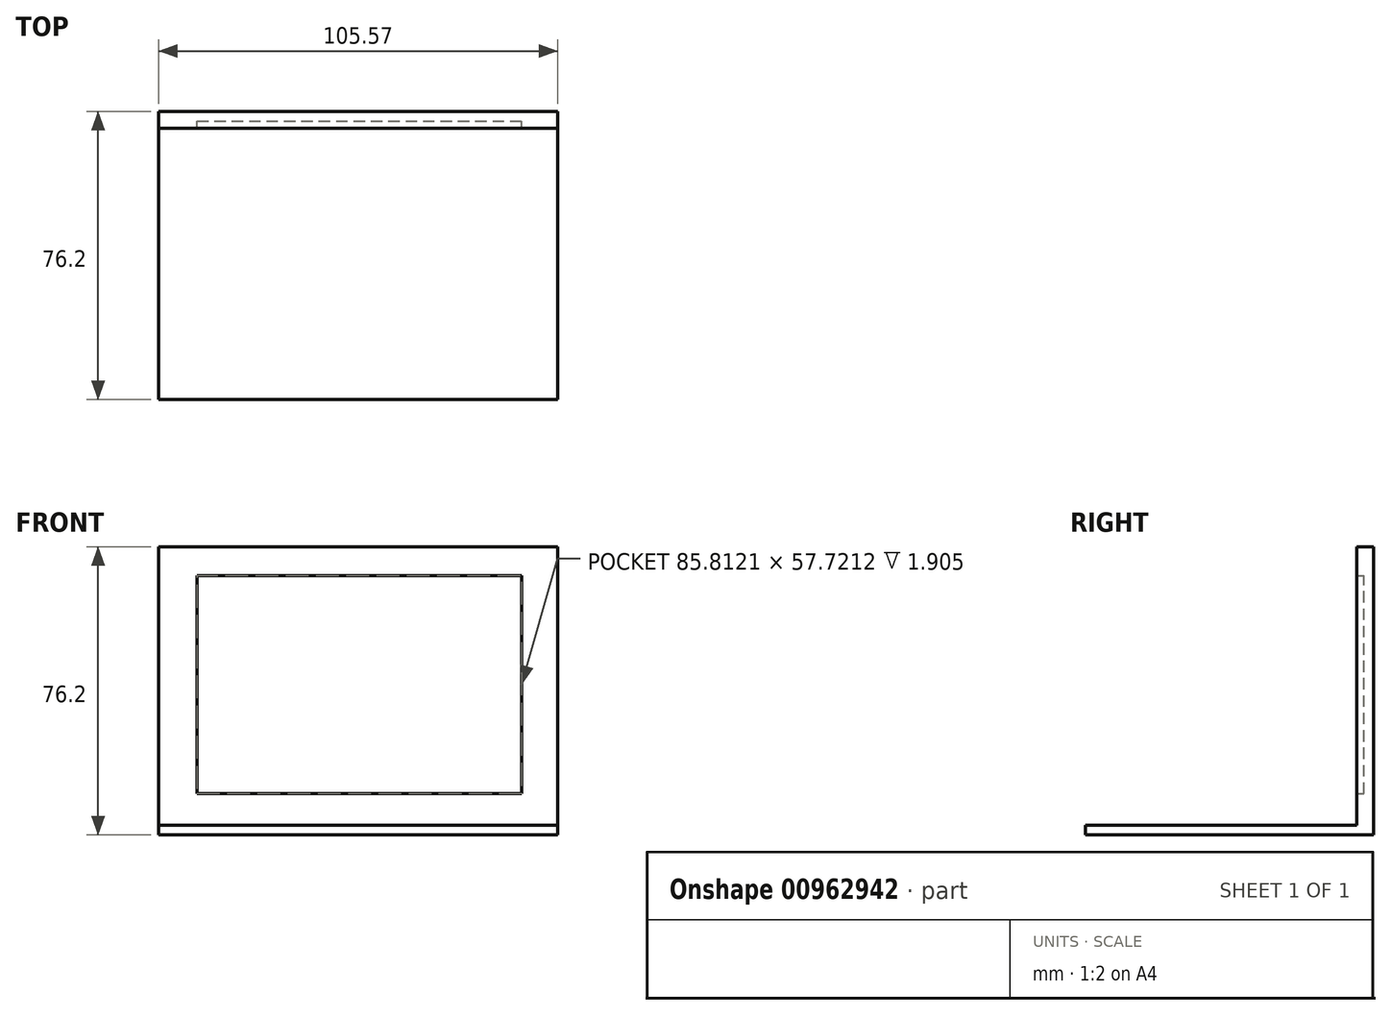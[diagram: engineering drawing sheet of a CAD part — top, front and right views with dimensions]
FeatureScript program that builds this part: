
annotation { "Feature Type Name" : "Feature", "Feature Type Description" : "" }
export const myFeature = defineFeature(function(context is Context, id is Id, definition is map)
    precondition{}
    {
        {
            var Q0;
            Q0=qCreatedBy(makeId("Top.planeOp"),FACE);
            var sketch = newSketch(context, id + "F0", { "sketchPlane" : qUnion([Q0])});
            skLineSegment(sketch, "E0.bottom", {"start": v(-45.25, -76.2) * mm, "end": v(60.32, -76.2) * mm});
            skLineSegment(sketch, "E0.top", {"start": v(-45.25, 0) * mm, "end": v(60.32, 0) * mm});
            skLineSegment(sketch, "E0.left", {"start": v(-45.25, -76.2) * mm, "end": v(-45.25, 0) * mm});
            skLineSegment(sketch, "E0.right", {"start": v(60.32, -76.2) * mm, "end": v(60.32, 0) * mm});
            skSolve(sketch);
        }
        {
            var Q0;
            Q0=makeQuery(id+"F0.imprint","IMPRINT",FACE,{"disambiguationData":[TD([[makeQuery(id+"F0.imprint","IMPRINT",EDGE,{"derivedFrom":sQuery(id+"F0.wireOp",EDGE,"E0.bottom")}),1.0]])]});
            extrude(context, id + "F1", {"entities" : qUnion([Q0]), "depth" : 76.2 * mm, "offsetDistance" : 25.4 * mm});
        }
        {
            var Q0;
            Q0=makeQuery(id+"F1.opExtrude","CAP_FACE",FACE,{"disambiguationData":[OSD([sQuery(id+"F0.wireOp",EDGE,"E0.bottom"),sQuery(id+"F0.wireOp",EDGE,"E0.top"),sQuery(id+"F0.wireOp",EDGE,"E0.left"),sQuery(id+"F0.wireOp",EDGE,"E0.right")])],"isStart":false});
            var Q1;
            Q1=makeQuery(id+"F1.opExtrude","SWEPT_FACE",FACE,{"disambiguationData":[OSD([sQuery(id+"F0.wireOp",EDGE,"E0.bottom")])]});
            var Q2;
            Q2=makeQuery(id+"F1.opExtrude","SWEPT_FACE",FACE,{"disambiguationData":[OSD([sQuery(id+"F0.wireOp",EDGE,"E0.left")])]});
            var Q3;
            Q3=makeQuery(id+"F1.opExtrude","SWEPT_FACE",FACE,{"disambiguationData":[OSD([sQuery(id+"F0.wireOp",EDGE,"E0.right")])]});
            shell(context, id + "F2", {"entities" : qUnion([Q0, Q1, Q2, Q3]), "thickness" : 2.54 * mm});
        }
        {
            var Q0;
            Q0=makeQuery(id+"F2.opShell","OFFSET_FACE",FACE,{"disambiguationData":[OSD([sQuery(id+"F0.wireOp",EDGE,"E0.top")])]});
            var sketch = newSketch(context, id + "F3", { "sketchPlane" : qUnion([Q0])});
            skLineSegment(sketch, "E1.bottom", {"start": v(-35.08, 10.89) * mm, "end": v(50.74, 10.89) * mm});
            skLineSegment(sketch, "E1.top", {"start": v(-35.08, 68.6) * mm, "end": v(50.74, 68.6) * mm});
            skLineSegment(sketch, "E1.left", {"start": v(-35.08, 10.89) * mm, "end": v(-35.08, 68.6) * mm});
            skLineSegment(sketch, "E1.right", {"start": v(50.74, 10.89) * mm, "end": v(50.74, 68.6) * mm});
            skSolve(sketch);
        }
        {
            var Q0;
            Q0=makeQuery(id+"F3.imprint","IMPRINT",FACE,{"disambiguationData":[TD([[makeQuery(id+"F3.imprint","IMPRINT",EDGE,{"derivedFrom":sQuery(id+"F3.wireOp",EDGE,"E1.bottom")}),-1.0]])]});
            extrude(context, id + "F4", {"entities" : qUnion([Q0]), "operationType" : NewBodyOperationType.ADD, "depth" : 1.9 * mm, "offsetDistance" : 25.4 * mm});
        }
    });
